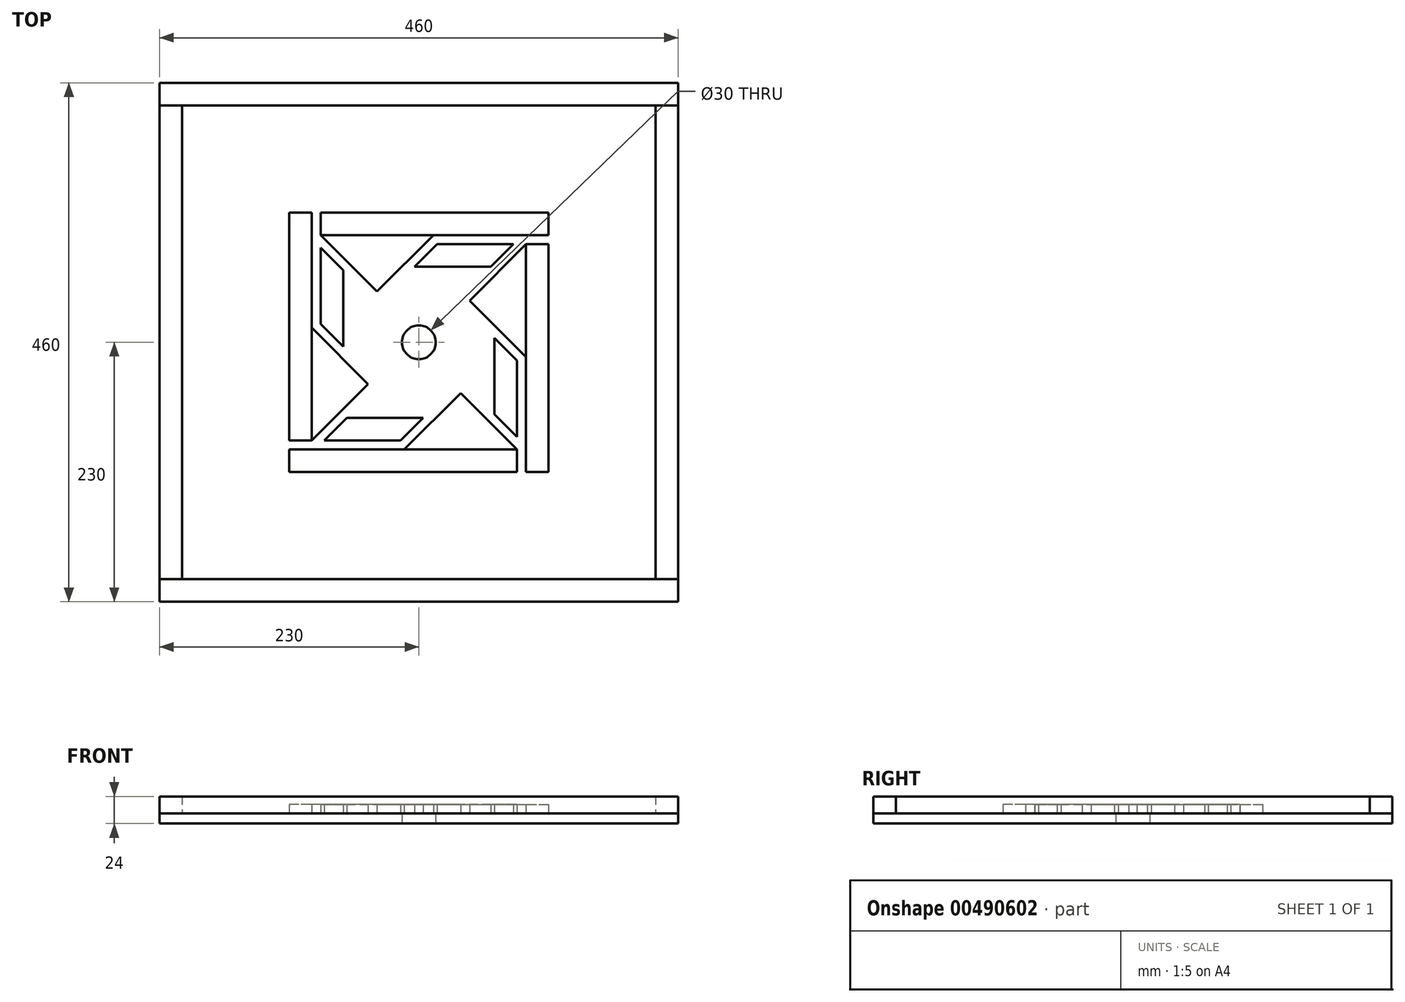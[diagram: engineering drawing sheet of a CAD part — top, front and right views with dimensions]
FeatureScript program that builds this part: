
annotation { "Feature Type Name" : "Feature", "Feature Type Description" : "" }
export const myFeature = defineFeature(function(context is Context, id is Id, definition is map)
    precondition{}
    {
        {
            var Q0;
            Q0=qCreatedBy(makeId("Top.planeOp"),FACE);
            var sketch = newSketch(context, id + "F0", { "sketchPlane" : qUnion([Q0])});
            skLineSegment(sketch, "E0.bottom", {"start": v(0, 0) * mm, "end": v(460, 0) * mm});
            skLineSegment(sketch, "E0.top", {"start": v(0, 460) * mm, "end": v(460, 460) * mm});
            skLineSegment(sketch, "E0.left", {"start": v(0, 0) * mm, "end": v(0, 460) * mm});
            skLineSegment(sketch, "E0.right", {"start": v(460, 0) * mm, "end": v(460, 460) * mm});
            skCircle(sketch, "E1", {"center": v(230, 230) * mm, "radius": 15 * mm});
            skSolve(sketch);
        }
        {
            var Q0;
            Q0 = qSketchRegion(id + "F0", true);
            extrude(context, id + "F1", {"entities" : qUnion([Q0]), "depth" : 9 * mm});
        }
        {
            var Q0;
            Q0=makeQuery(id+"F1.opExtrude","CAP_FACE",FACE,{"disambiguationData":[OSD([sQuery(id+"F0.wireOp",EDGE,"E0.bottom"),sQuery(id+"F0.wireOp",EDGE,"E0.top"),sQuery(id+"F0.wireOp",EDGE,"E0.left"),sQuery(id+"F0.wireOp",EDGE,"E0.right"),sQuery(id+"F0.wireOp",EDGE,"E1"),sQuery(id+"F0.wireOp",EDGE,"gQPfxJ8o-fLCM-IObb-tcAQ-c00SPKkZA4Ne"),sQuery(id+"F0.wireOp",EDGE,"CKRLOec6-3Qck-eF8W-hQeI-nCuMAZM72RUI"),sQuery(id+"F0.wireOp",EDGE,"cisOM2we-xoMo-1hqp-Q0wd-duupg42KSPbr"),sQuery(id+"F0.wireOp",EDGE,"4EDW4SaR-B43p-ACX8-lqq9-W5vOmygDVKjB"),sQuery(id+"F0.wireOp",EDGE,"jPt5dwkj-yVBJ-oe8B-bdRU-TzjszeuVTo3g"),sQuery(id+"F0.wireOp",EDGE,"adHI0qNB-wrY2-synv-m4an-OQYpOCalxEcK"),sQuery(id+"F0.wireOp",EDGE,"M3lPfnx5-vl0y-x3lH-Mq4J-kZeHz7g30DZP"),sQuery(id+"F0.wireOp",EDGE,"zQOZ9gWd-Em7E-tXni-Fwej-W4VEzmQNAwDv"),sQuery(id+"F0.wireOp",EDGE,"RbH4lk3t-i62x-I9MI-iKe0-Kw7EZqE7pTPU"),sQuery(id+"F0.wireOp",EDGE,"AsTSZmRx-7nzM-zCon-Ib6s-uOy5TMr0tiJ5"),sQuery(id+"F0.wireOp",EDGE,"74e7cc58-5b7d-495e-88bb-62de6cfef683.1.1"),sQuery(id+"F0.wireOp",EDGE,"74e7cc58-5b7d-495e-88bb-62de6cfef683.1.2"),sQuery(id+"F0.wireOp",EDGE,"74e7cc58-5b7d-495e-88bb-62de6cfef683.1.3"),sQuery(id+"F0.wireOp",EDGE,"74e7cc58-5b7d-495e-88bb-62de6cfef683.1.5"),sQuery(id+"F0.wireOp",EDGE,"74e7cc58-5b7d-495e-88bb-62de6cfef683.1.6"),sQuery(id+"F0.wireOp",EDGE,"74e7cc58-5b7d-495e-88bb-62de6cfef683.1.7"),sQuery(id+"F0.wireOp",EDGE,"74e7cc58-5b7d-495e-88bb-62de6cfef683.1.8"),sQuery(id+"F0.wireOp",EDGE,"74e7cc58-5b7d-495e-88bb-62de6cfef683.1.9"),sQuery(id+"F0.wireOp",EDGE,"74e7cc58-5b7d-495e-88bb-62de6cfef683.2.1"),sQuery(id+"F0.wireOp",EDGE,"74e7cc58-5b7d-495e-88bb-62de6cfef683.2.2"),sQuery(id+"F0.wireOp",EDGE,"74e7cc58-5b7d-495e-88bb-62de6cfef683.2.3"),sQuery(id+"F0.wireOp",EDGE,"74e7cc58-5b7d-495e-88bb-62de6cfef683.2.5"),sQuery(id+"F0.wireOp",EDGE,"74e7cc58-5b7d-495e-88bb-62de6cfef683.2.6"),sQuery(id+"F0.wireOp",EDGE,"74e7cc58-5b7d-495e-88bb-62de6cfef683.2.7"),sQuery(id+"F0.wireOp",EDGE,"74e7cc58-5b7d-495e-88bb-62de6cfef683.2.8"),sQuery(id+"F0.wireOp",EDGE,"74e7cc58-5b7d-495e-88bb-62de6cfef683.2.9"),sQuery(id+"F0.wireOp",EDGE,"74e7cc58-5b7d-495e-88bb-62de6cfef683.3.1"),sQuery(id+"F0.wireOp",EDGE,"74e7cc58-5b7d-495e-88bb-62de6cfef683.3.2"),sQuery(id+"F0.wireOp",EDGE,"74e7cc58-5b7d-495e-88bb-62de6cfef683.3.3"),sQuery(id+"F0.wireOp",EDGE,"74e7cc58-5b7d-495e-88bb-62de6cfef683.3.5"),sQuery(id+"F0.wireOp",EDGE,"74e7cc58-5b7d-495e-88bb-62de6cfef683.3.6"),sQuery(id+"F0.wireOp",EDGE,"74e7cc58-5b7d-495e-88bb-62de6cfef683.3.7"),sQuery(id+"F0.wireOp",EDGE,"74e7cc58-5b7d-495e-88bb-62de6cfef683.3.8"),sQuery(id+"F0.wireOp",EDGE,"74e7cc58-5b7d-495e-88bb-62de6cfef683.3.9"),sQuery(id+"F0.wireOp",EDGE,"99f87db0-aa3b-4e61-9036-f7877e163fca.0"),sQuery(id+"F0.wireOp",EDGE,"0d338c14-972f-415f-b20b-a500aa5d4484.1.0"),sQuery(id+"F0.wireOp",EDGE,"0d338c14-972f-415f-b20b-a500aa5d4484.1.1"),sQuery(id+"F0.wireOp",EDGE,"0d338c14-972f-415f-b20b-a500aa5d4484.1.2"),sQuery(id+"F0.wireOp",EDGE,"0d338c14-972f-415f-b20b-a500aa5d4484.2.0"),sQuery(id+"F0.wireOp",EDGE,"0d338c14-972f-415f-b20b-a500aa5d4484.2.1"),sQuery(id+"F0.wireOp",EDGE,"0d338c14-972f-415f-b20b-a500aa5d4484.2.2"),sQuery(id+"F0.wireOp",EDGE,"0d338c14-972f-415f-b20b-a500aa5d4484.3.0"),sQuery(id+"F0.wireOp",EDGE,"0d338c14-972f-415f-b20b-a500aa5d4484.3.1"),sQuery(id+"F0.wireOp",EDGE,"0d338c14-972f-415f-b20b-a500aa5d4484.3.2")])],"isStart":false});
            var sketch = newSketch(context, id + "F2", { "sketchPlane" : qUnion([Q0])});
            skLineSegment(sketch, "E2", {"start": v(143, 345) * mm, "end": v(345, 345) * mm});
            skLineSegment(sketch, "E3", {"start": v(345, 345) * mm, "end": v(345, 325) * mm});
            skLineSegment(sketch, "E4", {"start": v(345, 325) * mm, "end": v(143, 325) * mm});
            skLineSegment(sketch, "E5", {"start": v(143, 325) * mm, "end": v(143, 345) * mm});
            skLineSegment(sketch, "E6", {"start": v(143.1, 324.9) * mm, "end": v(193, 275) * mm});
            skLineSegment(sketch, "E7", {"start": v(193, 275) * mm, "end": v(242.9, 324.9) * mm});
            skLineSegment(sketch, "E8", {"start": v(313.69, 317) * mm, "end": v(293.69, 297) * mm});
            skLineSegment(sketch, "E9", {"start": v(293.69, 297) * mm, "end": v(226.31, 297) * mm});
            skLineSegment(sketch, "E10", {"start": v(226.31, 297) * mm, "end": v(246.31, 317) * mm});
            skLineSegment(sketch, "E11", {"start": v(246.31, 317) * mm, "end": v(313.69, 317) * mm});
            skLineSegment(sketch, "E12.1.1", {"start": v(163, 226.31) * mm, "end": v(143, 246.31) * mm});
            skLineSegment(sketch, "E12.1.2", {"start": v(143, 313.69) * mm, "end": v(163, 293.69) * mm});
            skLineSegment(sketch, "E12.1.3", {"start": v(163, 293.69) * mm, "end": v(163, 226.31) * mm});
            skLineSegment(sketch, "E12.1.5", {"start": v(115, 143) * mm, "end": v(115, 345) * mm});
            skLineSegment(sketch, "E12.1.6", {"start": v(135, 143) * mm, "end": v(115, 143) * mm});
            skLineSegment(sketch, "E12.1.7", {"start": v(115, 345) * mm, "end": v(135, 345) * mm});
            skLineSegment(sketch, "E12.1.8", {"start": v(135, 345) * mm, "end": v(135, 143) * mm});
            skLineSegment(sketch, "E12.1.9", {"start": v(143, 246.31) * mm, "end": v(143, 313.69) * mm});
            skLineSegment(sketch, "E12.2.1", {"start": v(233.69, 163) * mm, "end": v(213.69, 143) * mm});
            skLineSegment(sketch, "E12.2.2", {"start": v(146.31, 143) * mm, "end": v(166.31, 163) * mm});
            skLineSegment(sketch, "E12.2.3", {"start": v(166.31, 163) * mm, "end": v(233.69, 163) * mm});
            skLineSegment(sketch, "E12.2.5", {"start": v(317, 115) * mm, "end": v(115, 115) * mm});
            skLineSegment(sketch, "E12.2.6", {"start": v(317, 135) * mm, "end": v(317, 115) * mm});
            skLineSegment(sketch, "E12.2.7", {"start": v(115, 115) * mm, "end": v(115, 135) * mm});
            skLineSegment(sketch, "E12.2.8", {"start": v(115, 135) * mm, "end": v(317, 135) * mm});
            skLineSegment(sketch, "E12.2.9", {"start": v(213.69, 143) * mm, "end": v(146.31, 143) * mm});
            skLineSegment(sketch, "E12.3.1", {"start": v(297, 233.69) * mm, "end": v(317, 213.69) * mm});
            skLineSegment(sketch, "E12.3.2", {"start": v(317, 146.31) * mm, "end": v(297, 166.31) * mm});
            skLineSegment(sketch, "E12.3.3", {"start": v(297, 166.31) * mm, "end": v(297, 233.69) * mm});
            skLineSegment(sketch, "E12.3.5", {"start": v(345, 317) * mm, "end": v(345, 115) * mm});
            skLineSegment(sketch, "E12.3.6", {"start": v(325, 317) * mm, "end": v(345, 317) * mm});
            skLineSegment(sketch, "E12.3.7", {"start": v(345, 115) * mm, "end": v(325, 115) * mm});
            skLineSegment(sketch, "E12.3.8", {"start": v(325, 115) * mm, "end": v(325, 317) * mm});
            skLineSegment(sketch, "E12.3.9", {"start": v(317, 213.69) * mm, "end": v(317, 146.31) * mm});
            skPoint(sketch, "E12.center", {"position": v(230, 230) * mm});
            skLineSegment(sketch, "E13.0", {"start": v(242.9, 324.9) * mm, "end": v(143.1, 324.9) * mm});
            skPoint(sketch, "E14.orphan", {"position": v(243, 325) * mm});
            skLineSegment(sketch, "E15.1.0", {"start": v(135.1, 242.9) * mm, "end": v(135.1, 143.1) * mm});
            skLineSegment(sketch, "E15.1.1", {"start": v(185, 193) * mm, "end": v(135.1, 242.9) * mm});
            skLineSegment(sketch, "E15.1.2", {"start": v(135.1, 143.1) * mm, "end": v(185, 193) * mm});
            skLineSegment(sketch, "E15.2.0", {"start": v(217.1, 135.1) * mm, "end": v(316.9, 135.1) * mm});
            skLineSegment(sketch, "E15.2.1", {"start": v(267, 185) * mm, "end": v(217.1, 135.1) * mm});
            skLineSegment(sketch, "E15.2.2", {"start": v(316.9, 135.1) * mm, "end": v(267, 185) * mm});
            skLineSegment(sketch, "E15.3.0", {"start": v(324.9, 217.1) * mm, "end": v(324.9, 316.9) * mm});
            skLineSegment(sketch, "E15.3.1", {"start": v(275, 267) * mm, "end": v(324.9, 217.1) * mm});
            skLineSegment(sketch, "E15.3.2", {"start": v(324.9, 316.9) * mm, "end": v(275, 267) * mm});
            skSolve(sketch);
        }
        {
            var Q0;
            Q0 = qSketchRegion(id + "F2", true);
            extrude(context, id + "F3", {"entities" : qUnion([Q0]), "depth" : 8 * mm});
        }
        {
            var Q0;
            Q0=makeQuery(id+"F1.opExtrude","CAP_FACE",FACE,{"disambiguationData":[OSD([sQuery(id+"F0.wireOp",EDGE,"E0.bottom"),sQuery(id+"F0.wireOp",EDGE,"E0.top"),sQuery(id+"F0.wireOp",EDGE,"E0.left"),sQuery(id+"F0.wireOp",EDGE,"E0.right"),sQuery(id+"F0.wireOp",EDGE,"E1")])],"isStart":false});
            var sketch = newSketch(context, id + "F4", { "sketchPlane" : qUnion([Q0])});
            skLineSegment(sketch, "E16.1", {"start": v(0, 460) * mm, "end": v(460, 460) * mm});
            skLineSegment(sketch, "E16.3", {"start": v(0, 0) * mm, "end": v(460, 0) * mm});
            skLineSegment(sketch, "E17.0", {"start": v(0, 440) * mm, "end": v(460, 440) * mm});
            skLineSegment(sketch, "E18.0", {"start": v(0, 20) * mm, "end": v(460, 20) * mm});
            skLineSegment(sketch, "E19", {"start": v(0, 460) * mm, "end": v(0, 440) * mm});
            skLineSegment(sketch, "E20", {"start": v(460, 460) * mm, "end": v(460, 440) * mm});
            skLineSegment(sketch, "E21", {"start": v(460, 0) * mm, "end": v(460, 20) * mm});
            skLineSegment(sketch, "E22", {"start": v(0, 20) * mm, "end": v(0, 0) * mm});
            skLineSegment(sketch, "E23.0", {"start": v(0, 439.9) * mm, "end": v(20, 439.9) * mm});
            skLineSegment(sketch, "E24.0", {"start": v(0, 20.1) * mm, "end": v(20, 20.1) * mm});
            skLineSegment(sketch, "E25", {"start": v(0, 439.9) * mm, "end": v(0, 20.1) * mm});
            skLineSegment(sketch, "E26", {"start": v(460, 20.1) * mm, "end": v(460, 439.9) * mm});
            skLineSegment(sketch, "E27.0", {"start": v(20, 439.9) * mm, "end": v(20, 20.1) * mm});
            skLineSegment(sketch, "E28.0", {"start": v(440, 20.1) * mm, "end": v(440, 439.9) * mm});
            skLineSegment(sketch, "E29.trimOffspring", {"start": v(440, 439.9) * mm, "end": v(460, 439.9) * mm});
            skLineSegment(sketch, "E30.trimOffspring", {"start": v(440, 20.1) * mm, "end": v(460, 20.1) * mm});
            skSolve(sketch);
        }
        {
            var Q0;
            Q0 = qSketchRegion(id + "F4", true);
            extrude(context, id + "F5", {"entities" : qUnion([Q0]), "depth" : 15 * mm});
        }
    });
